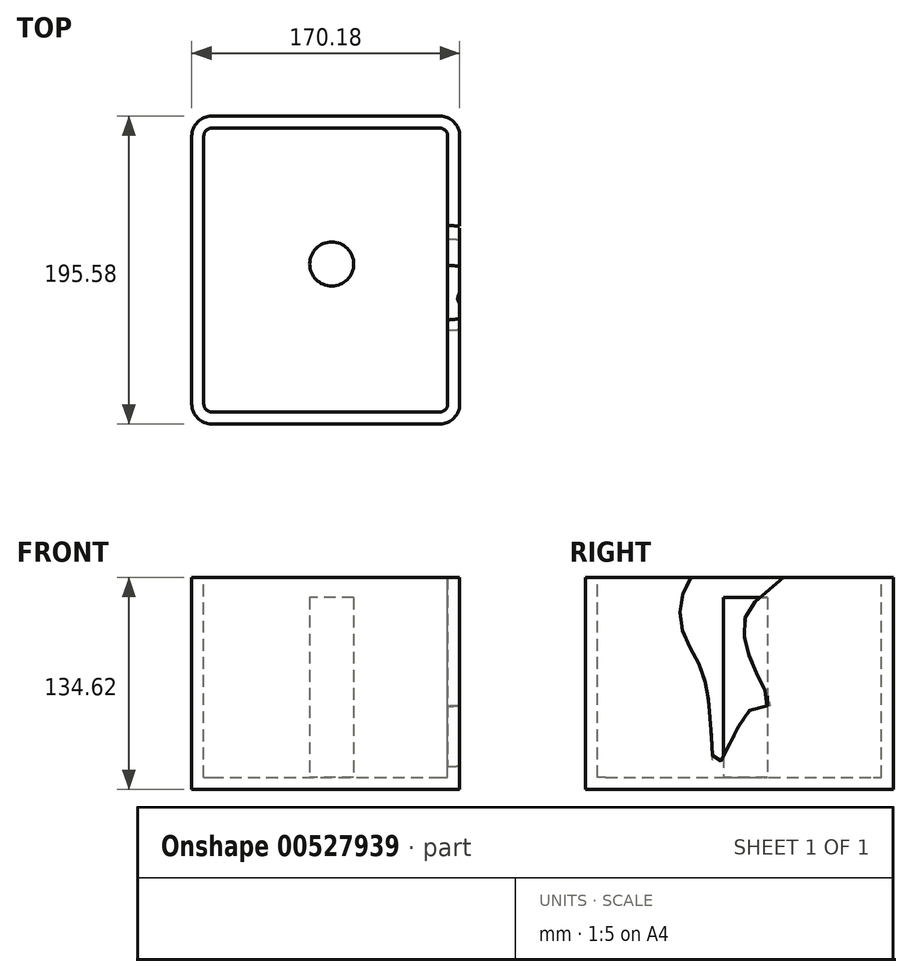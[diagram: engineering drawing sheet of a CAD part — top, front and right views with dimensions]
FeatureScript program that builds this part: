
annotation { "Feature Type Name" : "Feature", "Feature Type Description" : "" }
export const myFeature = defineFeature(function(context is Context, id is Id, definition is map)
    precondition{}
    {
        {
            var Q0;
            Q0=qCreatedBy(makeId("Top.planeOp"),FACE);
            var sketch = newSketch(context, id + "F0", { "sketchPlane" : qUnion([Q0])});
            skLineSegment(sketch, "E0.bottom", {"start": v(-63.5, -76.2) * mm, "end": v(81.28, -76.2) * mm});
            skLineSegment(sketch, "E0.top", {"start": v(-63.5, 119.38) * mm, "end": v(81.28, 119.38) * mm});
            skLineSegment(sketch, "E0.left", {"start": v(-76.2, -63.5) * mm, "end": v(-76.2, 106.68) * mm});
            skLineSegment(sketch, "E0.right", {"start": v(93.98, -63.5) * mm, "end": v(93.98, 106.68) * mm});
            skArc(sketch, "E1.filletArc", {"start": v(-63.5, 119.38) * mm, "mid": v(-72.48, 115.66) * mm, "end": v(-76.2, 106.68) * mm});
            skArc(sketch, "E2.filletArc", {"start": v(-76.2, -63.5) * mm, "mid": v(-72.48, -72.48) * mm, "end": v(-63.5, -76.2) * mm});
            skArc(sketch, "E3.filletArc", {"start": v(81.28, -76.2) * mm, "mid": v(90.26, -72.48) * mm, "end": v(93.98, -63.5) * mm});
            skArc(sketch, "E4.filletArc", {"start": v(93.98, 106.68) * mm, "mid": v(90.26, 115.66) * mm, "end": v(81.28, 119.38) * mm});
            skSolve(sketch);
        }
        {
            var Q0;
            Q0=makeQuery(id+"F0.imprint","IMPRINT",FACE,{"disambiguationData":[TD([[makeQuery(id+"F0.imprint","IMPRINT",EDGE,{"derivedFrom":sQuery(id+"F0.wireOp",EDGE,"E0.bottom")}),1.0]])]});
            extrude(context, id + "F1", {"entities" : qUnion([Q0]), "depth" : 127 * mm, "offsetDistance" : 25.4 * mm, "hasSecondDirection" : true, "secondDirectionOppositeDirection" : true, "secondDirectionDepth" : 7.62 * mm});
        }
        {
            var Q0;
            Q0=makeQuery(id+"F1.opExtrude","CAP_FACE",FACE,{"disambiguationData":[OSD([sQuery(id+"F0.wireOp",EDGE,"E0.bottom"),sQuery(id+"F0.wireOp",EDGE,"E0.top"),sQuery(id+"F0.wireOp",EDGE,"E0.left"),sQuery(id+"F0.wireOp",EDGE,"E0.right"),sQuery(id+"F0.wireOp",EDGE,"E1.filletArc"),sQuery(id+"F0.wireOp",EDGE,"E2.filletArc"),sQuery(id+"F0.wireOp",EDGE,"E3.filletArc"),sQuery(id+"F0.wireOp",EDGE,"E4.filletArc")])],"isStart":false});
            shell(context, id + "F2", {"entities" : qUnion([Q0]), "thickness" : 7.62 * mm});
        }
        {
            var Q0;
            Q0=makeQuery(id+"F1.opExtrude","SWEPT_FACE",FACE,{"disambiguationData":[OSD([sQuery(id+"F0.wireOp",EDGE,"E0.right")])]});
            var sketch = newSketch(context, id + "F3", { "sketchPlane" : qUnion([Q0])});
            skFitSpline(sketch, "E5", {"points": [v(0, 127) * mm, v(-10.36, 126.18) * mm, v(-15.87, 97.8) * mm, v(0, 59.38) * mm, v(7.03, 7.3) * mm, v(29.99, 44.39) * mm, v(40.61, 45.67) * mm, v(32.94, 65.01) * mm, v(27.98, 107.83) * mm, v(49.47, 127) * mm, v(0, 127) * mm]});
            skSolve(sketch);
        }
        {
            var Q0;
            {var subQ0=sQuery(id+"F3.wireOp",EDGE,"E5");var subQ1=makeQuery(id+"F1.opExtrude","CAP_EDGE",EDGE,{"disambiguationData":[OSD([sQuery(id+"F0.wireOp",EDGE,"E0.right")])],"isStart":false});var subQ2=makeQuery(id+"F3.imprint","INTERSECT",VERTEX,{"disambiguationData":[OD(0.0)],"derivedFrom":[subQ1,subQ0]});Q0=makeQuery(id+"F3.imprint","IMPRINT",FACE,{"disambiguationData":[TD([[makeQuery(id+"F3.imprint","IMPRINT",EDGE,{"disambiguationData":[TD([[subQ2,-1.0]])],"derivedFrom":subQ0}),1.0]])]});}
            extrude(context, id + "F4", {"entities" : qUnion([Q0]), "operationType" : NewBodyOperationType.REMOVE, "oppositeDirection" : true, "depth" : 25.4 * mm, "offsetDistance" : 25.4 * mm, "hasDraft" : true, "draftAngle" : 3 * degree});
        }
        {
            var Q0;
            Q0=makeQuery(id+"F2.opShell","OFFSET_FACE",FACE,{"disambiguationData":[OSD([sQuery(id+"F0.wireOp",EDGE,"E0.bottom"),sQuery(id+"F0.wireOp",EDGE,"E0.top"),sQuery(id+"F0.wireOp",EDGE,"E0.left"),sQuery(id+"F0.wireOp",EDGE,"E0.right"),sQuery(id+"F0.wireOp",EDGE,"E1.filletArc"),sQuery(id+"F0.wireOp",EDGE,"E2.filletArc"),sQuery(id+"F0.wireOp",EDGE,"E3.filletArc"),sQuery(id+"F0.wireOp",EDGE,"E4.filletArc")])]});
            var sketch = newSketch(context, id + "F5", { "sketchPlane" : qUnion([Q0])});
            skCircle(sketch, "E6", {"center": v(12.7, 25.4) * mm, "radius": 13.97 * mm});
            skSolve(sketch);
        }
        {
            var Q0;
            Q0=makeQuery(id+"F5.imprint","IMPRINT",FACE,{"disambiguationData":[TD([[makeQuery(id+"F5.imprint","IMPRINT",EDGE,{"derivedFrom":sQuery(id+"F5.wireOp",EDGE,"E6")}),1.0]])]});
            extrude(context, id + "F6", {"entities" : qUnion([Q0]), "operationType" : NewBodyOperationType.ADD, "depth" : 114.3 * mm, "offsetDistance" : 25.4 * mm});
        }
    });
